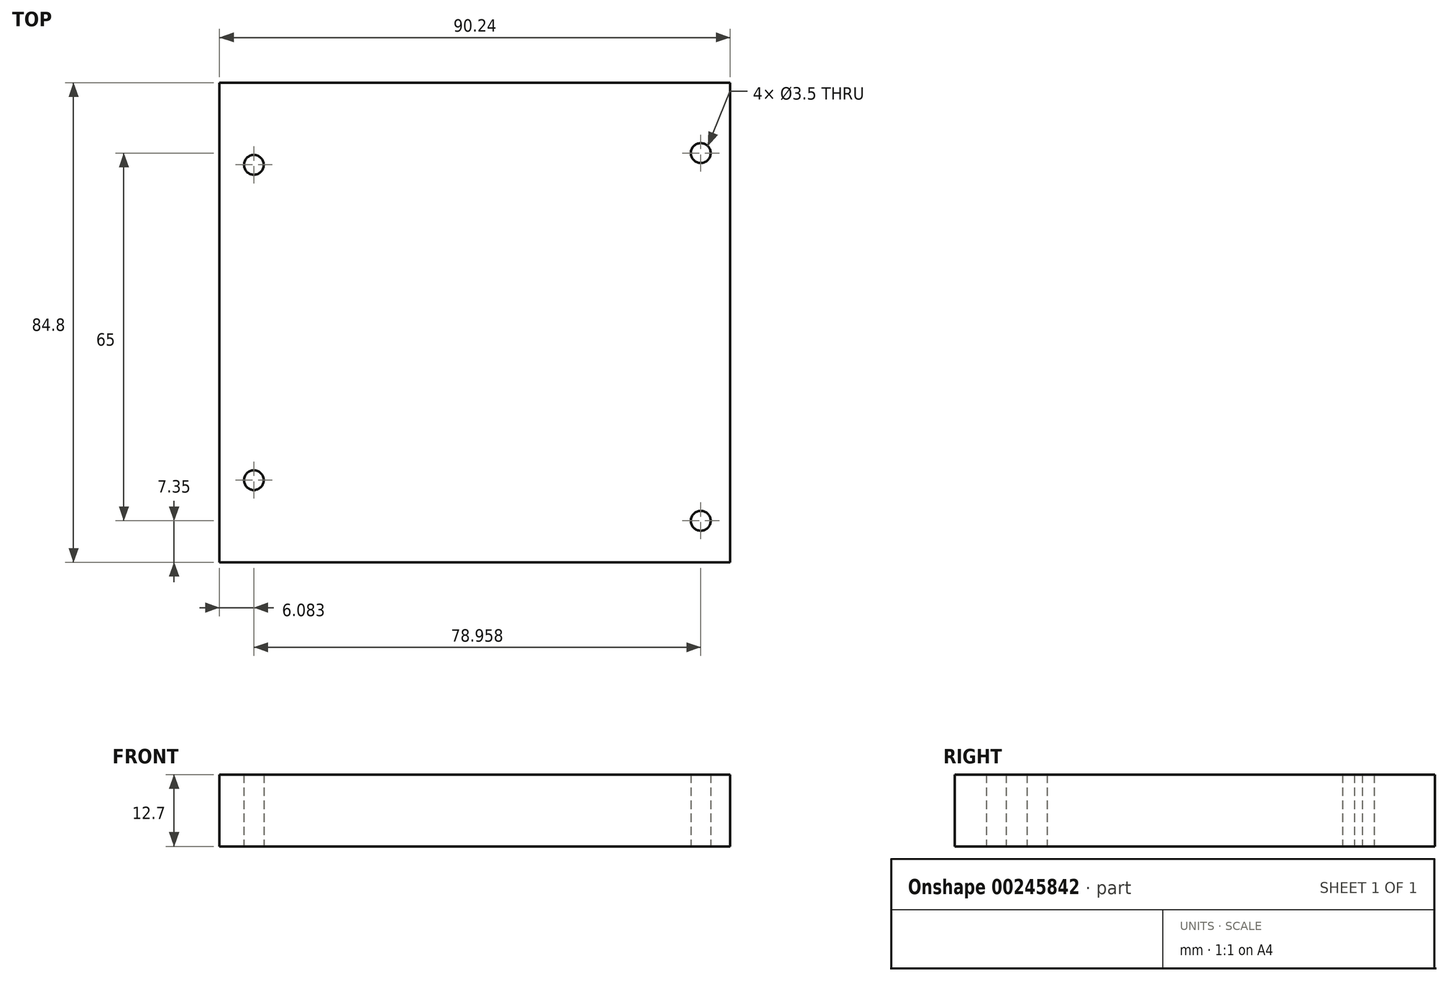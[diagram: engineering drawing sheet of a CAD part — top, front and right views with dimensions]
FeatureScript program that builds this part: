
annotation { "Feature Type Name" : "Feature", "Feature Type Description" : "" }
export const myFeature = defineFeature(function(context is Context, id is Id, definition is map)
    precondition{}
    {
        {
            var Q0;
            Q0=qCreatedBy(makeId("Top.planeOp"),FACE);
            var sketch = newSketch(context, id + "F0", { "sketchPlane" : qUnion([Q0])});
            skLineSegment(sketch, "E0.bottom", {"start": v(-45.12, 42.4) * mm, "end": v(45.13, 42.4) * mm});
            skLineSegment(sketch, "E0.top", {"start": v(-45.13, -42.4) * mm, "end": v(45.12, -42.4) * mm});
            skLineSegment(sketch, "E0.left", {"start": v(-45.12, 42.4) * mm, "end": v(-45.13, -42.4) * mm});
            skLineSegment(sketch, "E0.right", {"start": v(45.13, 42.4) * mm, "end": v(45.12, -42.4) * mm});
            skPoint(sketch, "E0.middle", {"position": v(0, 0) * mm});
            skCircle(sketch, "E1", {"center": v(39.92, 29.95) * mm, "radius": 1.75 * mm});
            skCircle(sketch, "E2", {"center": v(39.92, -35.05) * mm, "radius": 1.75 * mm});
            skCircle(sketch, "E3", {"center": v(-39.04, -27.87) * mm, "radius": 1.75 * mm});
            skCircle(sketch, "E4.MirrorC", {"center": v(-39.04, 27.87) * mm, "radius": 1.75 * mm});
            skSolve(sketch);
        }
        {
            var Q0;
            Q0=makeQuery(id+"F0.imprint","IMPRINT",FACE,{"disambiguationData":[TD([[makeQuery(id+"F0.imprint","IMPRINT",EDGE,{"derivedFrom":sQuery(id+"F0.wireOp",EDGE,"E0.bottom")}),-1.0]])]});
            extrude(context, id + "F1", {"entities" : qUnion([Q0]), "depth" : 12.7 * mm});
        }
    });
